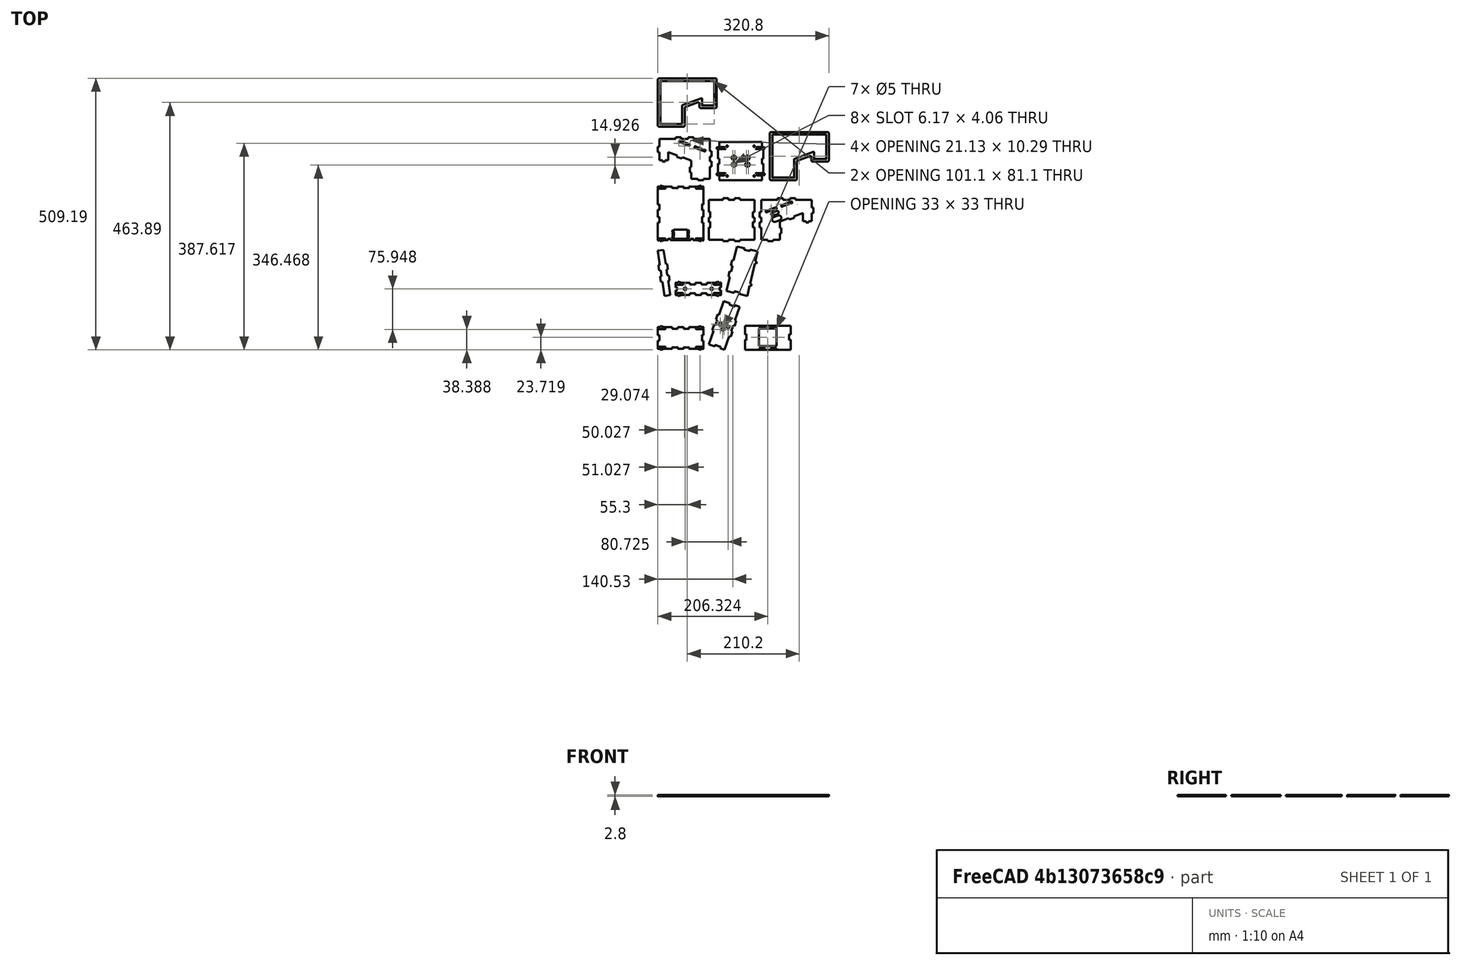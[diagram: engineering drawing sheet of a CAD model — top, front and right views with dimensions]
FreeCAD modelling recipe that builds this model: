
FCSTD DOCUMENT  (FreeCAD 0.21R33771 (Git))
Label: TheThing_v2_tabs_export
License: CERN Open Hardware Licence permissive
LicenseURL: https://cern-ohl.web.cern.ch/
objects: Part::Part2DObjectPython×14, Part::Feature×13, Sketcher::SketchObject×1
note: 28 computed .brp shape members not serialized (recipe doc carries the construction recipe); baked Part::Feature solids carry a one-line shape summary decoded from their .brp

FEATURE [Part::Feature] test
  Placement = pos=(42.8,39.3508,-27.5887) rot=(-1,0,0;1.5708rad)
  shape: bbox 85.6 x 44.36 x 2.8 mm, 94 faces (baked)
FEATURE [Part::Feature] test001
  Placement = pos=(164.106,31.7154,33.1277) rot=(0,0,0;3.14159rad)
  shape: bbox 57.92 x 91.16 x 2.8 mm, 39 faces (baked)
FEATURE [Part::Feature] test002
  Placement = pos=(206.323,8.47986,8.05) rot=(-0.939693,0,0;1.22173rad)
  shape: bbox 85.6 x 45.69 x 2.923 mm, 58 faces (baked)
FEATURE [Part::Feature] test003
  Placement = pos=(28.5232,146.767,73.3277) rot=(0,0,0;3.14159rad)
  shape: bbox 23.23 x 86.29 x 2.8 mm, 22 faces (baked)
FEATURE [Part::Feature] test004
  Placement = pos=(76.0272,62.5087,7.41128) rot=(-1,0,0;1.5708rad)
  shape: bbox 85.6 x 26.36 x 2.8 mm, 96 faces (baked)
FEATURE [Part::Feature] test005
  Placement = pos=(160.599,146.804,93.1277) rot=(0,0,0;3.14159rad)
  shape: bbox 58.5 x 92.48 x 2.8 mm, 34 faces (baked)
FEATURE [Part::Feature] test006
  Placement = pos=(42.8,268.64,12.5887) rot=(1,0,0;1.5708rad)
  shape: bbox 85.6 x 104.4 x 2.8 mm, 124 faces (baked)
FEATURE [Part::Feature] test007
  Placement = pos=(138.4,264.022,67.4723) rot=(0,0,1;0rad)
  shape: bbox 85.6 x 80.6 x 2.8 mm, 46 faces (baked)
FEATURE [Part::Feature] test008
  Placement = pos=(228.672,264.022,72.8) rot=(0,1,0;1.5708rad)
  shape: bbox 100.6 x 80.6 x 2.8 mm, 86 faces (baked)
FEATURE [Part::Feature] test009
  Placement = pos=(63.1277,378.379,72.8) rot=(0,-1,0;1.5708rad)
  shape: bbox 100.6 x 80.6 x 2.8 mm, 78 faces (baked)
FEATURE [Part::Feature] test010
  Placement = pos=(155.4,353.931,35.6) rot=(-0.939693,0,0;1.22173rad)
  shape: bbox 89.6 x 71.88 x 2.8 mm, 134 faces (baked)
FEATURE [Part::Feature] test011
  Placement = pos=(252.672,383.379,70.8) rot=(0,1,0;1.5708rad)
  shape: bbox 110.6 x 90.6 x 2.8 mm, 46 faces (baked)
FEATURE [Part::Feature] test012
  Placement = pos=(42.4723,483.979,70.8) rot=(0,1,0;1.5708rad)
  shape: bbox 110.6 x 90.6 x 2.8 mm, 46 faces (baked)
FEATURE [Part::Part2DObjectPython] Shape2DView  # Draft 2D object (typed FeaturePython)
  AutoUpdate = true
  Base = -> test
  Clip = false
  FuseArch = false
  HiddenLines = false
  InPlace = true
  OnlySolids = false
  Projection = (0,0,1)
  ProjectionMode = 0
  SegmentLength = 0.05
  Tessellation = false
  VisibleOnly = false
FEATURE [Part::Part2DObjectPython] Shape2DView001  # Draft 2D object (typed FeaturePython)
  AutoUpdate = true
  Base = -> test001
  Clip = false
  FuseArch = false
  HiddenLines = false
  InPlace = true
  OnlySolids = false
  Placement = pos=(127,-41,0) rot=(0,0,1;1.90799rad)
  Projection = (0,0,1)
  ProjectionMode = 0
  SegmentLength = 0.05
  Tessellation = false
  VisibleOnly = false
FEATURE [Part::Part2DObjectPython] Shape2DView002  # Draft 2D object (typed FeaturePython)
  AutoUpdate = true
  Base = -> test002
  Clip = false
  FuseArch = false
  HiddenLines = false
  InPlace = true
  OnlySolids = false
  Projection = (0,0,1)
  ProjectionMode = 0
  SegmentLength = 0.05
  Tessellation = false
  VisibleOnly = false
FEATURE [Part::Part2DObjectPython] Shape2DView003  # Draft 2D object (typed FeaturePython)
  AutoUpdate = true
  Base = -> test003
  Clip = false
  FuseArch = false
  HiddenLines = false
  InPlace = true
  OnlySolids = false
  Placement = pos=(183.95,101.66,0) rot=(0,0,-1;4.85708rad)
  Projection = (0,0,1)
  ProjectionMode = 0
  SegmentLength = 0.05
  Tessellation = false
  VisibleOnly = false
FEATURE [Part::Part2DObjectPython] Shape2DView004  # Draft 2D object (typed FeaturePython)
  AutoUpdate = true
  Base = -> test004
  Clip = false
  FuseArch = false
  HiddenLines = false
  InPlace = true
  OnlySolids = false
  Placement = pos=(-33.3,40,0) rot=(0,0,1;0rad)
  Projection = (0,0,1)
  ProjectionMode = 0
  SegmentLength = 0.05
  Tessellation = false
  VisibleOnly = false
FEATURE [Part::Part2DObjectPython] Shape2DView005  # Draft 2D object (typed FeaturePython)
  AutoUpdate = true
  Base = -> test005
  Clip = false
  FuseArch = false
  HiddenLines = false
  InPlace = true
  OnlySolids = false
  Placement = pos=(222.4,69,0) rot=(0,0,1;1.80135rad)
  Projection = (0,0,1)
  ProjectionMode = 0
  SegmentLength = 0.05
  Tessellation = false
  VisibleOnly = false
FEATURE [Part::Part2DObjectPython] Shape2DView006  # Draft 2D object (typed FeaturePython)
  AutoUpdate = true
  Base = -> test006
  Clip = false
  FuseArch = false
  HiddenLines = false
  InPlace = true
  OnlySolids = false
  Placement = pos=(0,7,0) rot=(0,0,1;0rad)
  Projection = (0,0,1)
  ProjectionMode = 0
  SegmentLength = 0.05
  Tessellation = false
  VisibleOnly = false
FEATURE [Part::Part2DObjectPython] Shape2DView007  # Draft 2D object (typed FeaturePython)
  AutoUpdate = true
  Base = -> test007
  Clip = false
  FuseArch = false
  HiddenLines = false
  InPlace = true
  OnlySolids = false
  Placement = pos=(0,30,0) rot=(0,0,1;0rad)
  Projection = (0,0,1)
  ProjectionMode = 0
  SegmentLength = 0.05
  Tessellation = false
  VisibleOnly = false
FEATURE [Part::Part2DObjectPython] Shape2DView008  # Draft 2D object (typed FeaturePython)
  AutoUpdate = true
  Base = -> test008
  Clip = false
  FuseArch = false
  HiddenLines = false
  InPlace = true
  OnlySolids = false
  Placement = pos=(-96,-125,0) rot=(0,0,1;0rad)
  Projection = (0,0,1)
  ProjectionMode = 0
  SegmentLength = 0.05
  Tessellation = false
  VisibleOnly = false
FEATURE [Part::Part2DObjectPython] Shape2DView009  # Draft 2D object (typed FeaturePython)
  AutoUpdate = true
  Base = -> test009
  Clip = false
  FuseArch = false
  HiddenLines = false
  InPlace = true
  OnlySolids = false
  Placement = pos=(195.8,396,0) rot=(0,0,1;3.14159rad)
  Projection = (0,0,1)
  ProjectionMode = 0
  SegmentLength = 0.05
  Tessellation = false
  VisibleOnly = false
FEATURE [Part::Part2DObjectPython] Shape2DView010  # Draft 2D object (typed FeaturePython)
  AutoUpdate = true
  Base = -> test010
  Clip = false
  FuseArch = false
  HiddenLines = false
  InPlace = true
  OnlySolids = false
  Placement = pos=(-17,-157,0) rot=(0,0,1;0rad)
  Projection = (0,0,1)
  ProjectionMode = 0
  SegmentLength = 0.05
  Tessellation = false
  VisibleOnly = false
FEATURE [Part::Part2DObjectPython] Shape2DView011  # Draft 2D object (typed FeaturePython)
  AutoUpdate = true
  Base = -> test011
  Clip = false
  FuseArch = false
  HiddenLines = false
  InPlace = true
  OnlySolids = false
  Placement = pos=(463.4,456.7,0) rot=(0,0,1;3.14159rad)
  Projection = (0,0,1)
  ProjectionMode = 0
  SegmentLength = 0.05
  Tessellation = false
  VisibleOnly = false
FEATURE [Part::Part2DObjectPython] Shape2DView012  # Draft 2D object (typed FeaturePython)
  AutoUpdate = true
  Base = -> test012
  Clip = false
  FuseArch = false
  HiddenLines = false
  InPlace = true
  OnlySolids = false
  Placement = pos=(-231,255.3,0) rot=(0,0,1;4.71239rad)
  Projection = (0,0,1)
  ProjectionMode = 0
  SegmentLength = 0.05
  Tessellation = false
  VisibleOnly = false
FEATURE [Sketcher::SketchObject] Sketch
  FullyConstrained = false
  sketch-geometry (67):
    g0: LineSegment StartX=163.523 StartY=45.4002 StartZ=0 EndX=190.716 EndY=45.4002 EndZ=0
    g1: LineSegment StartX=200.53 StartY=45.4002 StartZ=0 EndX=212.116 EndY=45.4002 EndZ=0
    g2: LineSegment StartX=221.93 StartY=45.4002 StartZ=0 EndX=249.123 EndY=45.4002 EndZ=0
    g3: LineSegment StartX=163.523 StartY=28.6259 StartZ=0 EndX=163.523 EndY=45.4002 EndZ=0
    g4: LineSegment StartX=163.523 StartY=28.6259 StartZ=0 EndX=166.098 EndY=28.6259 EndZ=0
    g5: ArcOfCircle CenterX=166.27 CenterY=28.5263 CenterZ=0 NormalX=0 NormalY=0 NormalZ=1 AngleXU=-4e-16 Radius=0.19911 StartAngle=0 EndAngle=2.61799
    g6: ArcOfCircle CenterX=166.27 CenterY=28.5263 CenterZ=0 NormalX=0 NormalY=0 NormalZ=1 AngleXU=-4e-16 Radius=0.19911 StartAngle=5.23599 EndAngle=6.28319
    g7: LineSegment StartX=166.37 StartY=28.3539 StartZ=0 EndX=166.37 EndY=19.0846 EndZ=0
    g8: ArcOfCircle CenterX=166.27 CenterY=18.9121 CenterZ=0 NormalX=0 NormalY=0 NormalZ=1 AngleXU=-4e-16 Radius=0.19911 StartAngle=0 EndAngle=1.0472
    g9: ArcOfCircle CenterX=166.27 CenterY=18.9121 CenterZ=0 NormalX=0 NormalY=0 NormalZ=1 AngleXU=-4e-16 Radius=0.19911 StartAngle=3.66519 EndAngle=6.28319
    g10: LineSegment StartX=163.523 StartY=18.8126 StartZ=0 EndX=166.098 EndY=18.8126 EndZ=0
    g11: LineSegment StartX=163.523 StartY=6.22e-14 StartZ=0 EndX=163.523 EndY=18.8126 EndZ=0
    g12: LineSegment StartX=190.661 StartY=4.35e-14 StartZ=0 EndX=163.523 EndY=6.28e-14 EndZ=0
    g13: ArcOfEllipse CenterX=190.813 CenterY=-0.126709 CenterZ=0 NormalX=0 NormalY=0 NormalZ=1 MajorRadius=0.205266 MinorRadius=0.192887 AngleXU=1.5708 StartAngle=0.523599 EndAngle=0.905501
    g14: LineSegment StartX=190.716 StartY=2.56925 StartZ=0 EndX=190.716 EndY=0.0510565 EndZ=0
    g15: ArcOfEllipse CenterX=190.813 CenterY=2.74701 CenterZ=0 NormalX=0 NormalY=0 NormalZ=1 MajorRadius=0.205266 MinorRadius=0.192887 AngleXU=1.5708 StartAngle=1.5708 EndAngle=2.61799
    g16: ArcOfEllipse CenterX=190.813 CenterY=2.74701 CenterZ=0 NormalX=0 NormalY=0 NormalZ=1 MajorRadius=0.205266 MinorRadius=0.192887 AngleXU=1.5708 StartAngle=5.23599 EndAngle=7.85398
    g17: LineSegment StartX=200.266 StartY=2.84964 StartZ=0 EndX=190.98 EndY=2.84964 EndZ=0
    g18: ArcOfEllipse CenterX=200.433 CenterY=2.74701 CenterZ=0 NormalX=0 NormalY=0 NormalZ=1 MajorRadius=0.205266 MinorRadius=0.192887 AngleXU=1.5708 StartAngle=4.71239 EndAngle=7.33038
    g19: ArcOfEllipse CenterX=200.433 CenterY=2.74701 CenterZ=0 NormalX=0 NormalY=0 NormalZ=1 MajorRadius=0.205266 MinorRadius=0.192887 AngleXU=1.5708 StartAngle=3.66519 EndAngle=4.71239
    g20: LineSegment StartX=200.53 StartY=2.56925 StartZ=0 EndX=200.53 EndY=0.0510565 EndZ=0
    g21: ArcOfEllipse CenterX=200.433 CenterY=-0.126709 CenterZ=0 NormalX=0 NormalY=0 NormalZ=1 MajorRadius=0.205266 MinorRadius=0.192887 AngleXU=1.5708 StartAngle=5.37768 EndAngle=5.75959
    g22: LineSegment StartX=212.061 StartY=2.82e-14 StartZ=0 EndX=200.585 EndY=3.64e-14 EndZ=0
    g23: ArcOfEllipse CenterX=212.213 CenterY=-0.126709 CenterZ=0 NormalX=0 NormalY=0 NormalZ=1 MajorRadius=0.205266 MinorRadius=0.192887 AngleXU=1.5708 StartAngle=0.523599 EndAngle=0.905501
    g24: LineSegment StartX=212.116 StartY=2.56925 StartZ=0 EndX=212.116 EndY=0.0510565 EndZ=0
    g25: ArcOfEllipse CenterX=212.213 CenterY=2.74701 CenterZ=0 NormalX=0 NormalY=0 NormalZ=1 MajorRadius=0.205266 MinorRadius=0.192887 AngleXU=1.5708 StartAngle=1.5708 EndAngle=2.61799
    g26: ArcOfEllipse CenterX=212.213 CenterY=2.74701 CenterZ=0 NormalX=0 NormalY=0 NormalZ=1 MajorRadius=0.205266 MinorRadius=0.192887 AngleXU=1.5708 StartAngle=5.23599 EndAngle=7.85398
    g27: LineSegment StartX=221.666 StartY=2.84964 StartZ=0 EndX=212.38 EndY=2.84964 EndZ=0
    g28: ArcOfEllipse CenterX=221.833 CenterY=2.74701 CenterZ=0 NormalX=0 NormalY=0 NormalZ=1 MajorRadius=0.205266 MinorRadius=0.192887 AngleXU=1.5708 StartAngle=4.71239 EndAngle=7.33038
    g29: ArcOfEllipse CenterX=221.833 CenterY=2.74701 CenterZ=0 NormalX=0 NormalY=0 NormalZ=1 MajorRadius=0.205266 MinorRadius=0.192887 AngleXU=1.5708 StartAngle=3.66519 EndAngle=4.71239
    g30: LineSegment StartX=221.93 StartY=2.56925 StartZ=0 EndX=221.93 EndY=0.0510565 EndZ=0
    g31: ArcOfEllipse CenterX=221.833 CenterY=-0.126709 CenterZ=0 NormalX=0 NormalY=0 NormalZ=1 MajorRadius=0.205266 MinorRadius=0.192887 AngleXU=1.5708 StartAngle=5.37768 EndAngle=5.75959
    g32: LineSegment StartX=249.123 StartY=1.8e-15 StartZ=0 EndX=221.985 EndY=2.11e-14 EndZ=0
    g33: LineSegment StartX=249.123 StartY=18.8126 StartZ=0 EndX=249.123 EndY=2.84e-14 EndZ=0
    g34: LineSegment StartX=246.548 StartY=18.8126 StartZ=0 EndX=249.123 EndY=18.8126 EndZ=0
    g35: ArcOfCircle CenterX=246.376 CenterY=18.9121 CenterZ=0 NormalX=0 NormalY=0 NormalZ=1 AngleXU=-4e-16 Radius=0.19911 StartAngle=2.0944 EndAngle=5.75959
    g36: LineSegment StartX=246.276 StartY=28.3539 StartZ=0 EndX=246.276 EndY=19.0846 EndZ=0
    g37: ArcOfCircle CenterX=246.376 CenterY=28.5263 CenterZ=0 NormalX=0 NormalY=0 NormalZ=1 AngleXU=-4e-16 Radius=0.19911 StartAngle=0.523599 EndAngle=4.18879
    g38: LineSegment StartX=246.548 StartY=28.6259 StartZ=0 EndX=249.123 EndY=28.6259 EndZ=0
    g39: LineSegment StartX=249.123 StartY=45.4002 StartZ=0 EndX=249.123 EndY=28.6259 EndZ=0
    g40: LineSegment StartX=221.93 StartY=45.4002 StartZ=0 EndX=221.93 EndY=42.84 EndZ=0
    g41: ArcOfEllipse CenterX=221.83 CenterY=42.6565 CenterZ=0 NormalX=0 NormalY=0 NormalZ=1 MajorRadius=0.211888 MinorRadius=0.19911 AngleXU=1.5708 StartAngle=4.71239 EndAngle=5.75959
    g42: ArcOfEllipse CenterX=221.83 CenterY=42.6565 CenterZ=0 NormalX=0 NormalY=0 NormalZ=1 MajorRadius=0.211888 MinorRadius=0.19911 AngleXU=1.5708 StartAngle=4.44345 EndAngle=4.71239
    g43: LineSegment StartX=212.408 StartY=42.6002 StartZ=0 EndX=221.638 EndY=42.6002 EndZ=0
    g44: ArcOfEllipse CenterX=212.216 CenterY=42.6565 CenterZ=0 NormalX=0 NormalY=0 NormalZ=1 MajorRadius=0.21181 MinorRadius=0.199017 AngleXU=1.57066 StartAngle=1.5708 EndAngle=1.83973
    g45: ArcOfEllipse CenterX=212.216 CenterY=42.6565 CenterZ=0 NormalX=0 NormalY=0 NormalZ=1 MajorRadius=0.211888 MinorRadius=0.19911 AngleXU=1.5708 StartAngle=0.523599 EndAngle=1.5708
    g46: LineSegment StartX=212.116 StartY=45.4002 StartZ=0 EndX=212.116 EndY=42.84 EndZ=0
    g47: LineSegment StartX=200.53 StartY=45.4002 StartZ=0 EndX=200.53 EndY=42.84 EndZ=0
    g48: ArcOfEllipse CenterX=200.43 CenterY=42.6569 CenterZ=0 NormalX=0 NormalY=0 NormalZ=1 MajorRadius=0.211759 MinorRadius=0.19911 AngleXU=1.56888 StartAngle=4.71239 EndAngle=5.75959
    g49: ArcOfEllipse CenterX=200.43 CenterY=42.6565 CenterZ=0 NormalX=0 NormalY=0 NormalZ=1 MajorRadius=0.211888 MinorRadius=0.19911 AngleXU=1.57278 StartAngle=4.44345 EndAngle=4.71239
    g50: LineSegment StartX=191.008 StartY=42.6002 StartZ=0 EndX=200.238 EndY=42.6002 EndZ=0
    g51: ArcOfEllipse CenterX=190.816 CenterY=42.6565 CenterZ=0 NormalX=0 NormalY=0 NormalZ=1 MajorRadius=0.211889 MinorRadius=0.19911 AngleXU=1.5708 StartAngle=1.5708 EndAngle=1.83973
    g52: ArcOfEllipse CenterX=190.816 CenterY=42.6565 CenterZ=0 NormalX=0 NormalY=0 NormalZ=1 MajorRadius=0.211888 MinorRadius=0.19911 AngleXU=1.5708 StartAngle=0.523599 EndAngle=1.5708
    g53: LineSegment StartX=190.716 StartY=45.4002 StartZ=0 EndX=190.716 EndY=42.84 EndZ=0
    g54: ArcOfCircle CenterX=190.324 CenterY=39.7192 CenterZ=0 NormalX=0 NormalY=0 NormalZ=1 AngleXU=-7e-16 Radius=0.5 StartAngle=1.5708 EndAngle=3.14159
    g55: LineSegment StartX=190.324 StartY=40.2192 StartZ=0 EndX=222.324 EndY=40.2192 EndZ=0
    g56: LineSegment StartX=189.824 StartY=7.71924 StartZ=0 EndX=189.824 EndY=39.7192 EndZ=0
    g57: ArcOfCircle CenterX=222.324 CenterY=39.7192 CenterZ=0 NormalX=0 NormalY=0 NormalZ=1 AngleXU=-7e-16 Radius=0.5 StartAngle=-2.7e-15 EndAngle=1.5708
    g58: ArcOfCircle CenterX=190.324 CenterY=7.71924 CenterZ=0 NormalX=0 NormalY=0 NormalZ=1 AngleXU=-7e-16 Radius=0.5 StartAngle=3.14159 EndAngle=4.71239
    g59: LineSegment StartX=222.824 StartY=39.7192 StartZ=0 EndX=222.824 EndY=7.71924 EndZ=0
    g60: LineSegment StartX=222.324 StartY=7.21924 StartZ=0 EndX=190.324 EndY=7.21924 EndZ=0
    g61: ArcOfCircle CenterX=222.324 CenterY=7.71924 CenterZ=0 NormalX=0 NormalY=0 NormalZ=1 AngleXU=-7e-16 Radius=0.5 StartAngle=4.71239 EndAngle=6.28319
    g62: ArcOfCircle CenterX=200.43 CenterY=42.6569 CenterZ=0 NormalX=0 NormalY=0 NormalZ=1 AngleXU=0 Radius=0.200039 StartAngle=3.42888 EndAngle=5.99789
    g63: ArcOfCircle CenterX=190.816 CenterY=42.6565 CenterZ=0 NormalX=0 NormalY=0 NormalZ=1 AngleXU=0 Radius=0.200039 StartAngle=3.42689 EndAngle=5.99788
    g64: ArcOfCircle CenterX=212.216 CenterY=42.6565 CenterZ=0 NormalX=0 NormalY=0 NormalZ=1 AngleXU=0 Radius=0.199942 StartAngle=3.42689 EndAngle=5.99788
    g65: LineSegment StartX=200.622 StartY=42.6002 StartZ=0 EndX=200.622 EndY=42.6002 EndZ=0
    g66: ArcOfCircle CenterX=221.83 CenterY=42.6565 CenterZ=0 NormalX=0 NormalY=0 NormalZ=1 AngleXU=0 Radius=0.200039 StartAngle=3.42689 EndAngle=5.99788
  constraints (11):
    c: Coincident(g62,g48)
    c: Coincident(g62,g49)
    c: Coincident(g63,g51)
    c: Coincident(g64,g44)
    c: Coincident(g43,g64)
    c: Coincident(g50,g62)
    c: PointOnObject(g65,g62)
    c: Coincident(g50,g63)
    c: Coincident(g66,g41)
    c: Coincident(g66,g42)
    c: Coincident(g43,g66)
FEATURE [Part::Part2DObjectPython] Shape2DView013  # Draft 2D object (typed FeaturePython)
  AutoUpdate = true
  Base = -> Sketch
  Clip = false
  FuseArch = false
  HiddenLines = false
  InPlace = true
  OnlySolids = false
  Placement = pos=(-163.5,80,0) rot=(0,0,1;0rad)
  Projection = (0,0,1)
  ProjectionMode = 0
  SegmentLength = 0.05
  Tessellation = false
  VisibleOnly = false
